# Revit family: VIESSMANN - Vitocell 100-L (CVL.CVLA)
name_source: partatom
category: Wyposażenie mechaniczne
revit_build: Autodesk Revit 2017 (Build: 20160720_1515(x64)
units: mm (PartAtom-declared; Revit-internal decimal feet)

## family parameters
Numer OmniClass = 23.65.35.11.11
Oparty na płaszczyźnie roboczej = Nie
Punkt obliczania pomieszczeń = Nie
Tnij formami wycięć po wczytaniu = Tak
Typ części = Normalny
Tytuł OmniClass = Storage Water Heaters
Współdzielony = Nie
Wymiar okrągłego złącza = Użyj średnicy
Zawsze pionowo = Tak

## types (5) — shared parameters
Autor = https://www.archispace.pl
Ciepła woda użytkowa = 2"
Cyrkulacja = 1 1/4"
Klasa efektywności energetycznej = B
Numer identyfikacyjny produktu = 0256/08-13
Opis = Podgrzewacz pojemnościowy
Opis indeksowy = 0256/08-13
Producent = Viessmann Sp.z.o.o.
URL = https://www.viessmann-projektant.pl
Viessmann Kolor 1 = Viessmann Kolor 1
Viessmann Kolor 2 = Viessmann Kolor 2
Viessmann Kolor 3 = Viessmann Kolor 3
Wlot ciepłej wody użytkowej od strony wymiennika ciepła = 2"
Zimna woda użytkowa = 2"

## per-type parameters (varying)
- Zbiornik CVL 2000L: Ilość ciepła dyżurnego=4.55 kWh/24h; Masa całkowita=444.00 kg; Masa podgrzewacza=483.00 kg; Model=Podgrzewacz pojemnościowy Viessmann Vitocell 100-L CVL 2000L / Hot water storage tank Viessmann Vitocell 100-L CVL 2000L; Odpowietrzanie=1"; Podział=1310 mm  [stored 4.2979 ft]; Pojemność podgrzewacza=2000.0 L; Spust boczny=1 1/2"; Spust dolny=1"; Szerokośc z izolacją cieplną=1477 mm  [stored 4.8458 ft]; Szerokość - bez izolacji cieplnej=1346 mm  [stored 4.41601 ft]; Szerokość - z izolacją cieplną=1477 mm  [stored 4.8458 ft]; Wymiar przechylenia - bez izolacji cieplnej=2390 mm; Wysokośc przyłącza grzałki=564 mm; Wysokość - bez izolacji cieplnej=2392 mm; Wysokość - z izolacją cieplną=2479 mm; Wysokość króćca cwu=1970 mm; Wysokość króćca cwu/wc=1790 mm  [stored 5.8727 ft]; Wysokość króćca cyrkulacji=1603 mm  [stored 5.25919 ft]; Wysokość króćca spustu=124 mm  [stored 0.406824 ft]; Wysokość króćca zimnej wody użytkowej=511 mm; Wysokość z izolacją cieplną=2479 mm; Średnica - bez izolacji cieplnej=1100 mm; Średnica - z izolacją cieplną=1310 mm  [stored 4.2979 ft]; Średnica z izolacją cieplną=1310 mm  [stored 4.2979 ft]
- Zbiornik CVL 500L: Ilość ciepła dyżurnego=1.95 kWh/24h; Masa całkowita=136.00 kg; Masa podgrzewacza=156.00 kg; Model=Podgrzewacz pojemnościowy Viessmann Vitocell 100-L CVL 500L / Hot water storage tank Viessmann Vitocell 100-L CVL 500L; Odpowietrzanie=0"; Podział=859 mm  [stored 2.81824 ft]; Pojemność podgrzewacza=500.0 L; Spust boczny=1 1/4"; Spust dolny=0"; Szerokośc z izolacją cieplną=923 mm  [stored 3.02822 ft]; Szerokość - bez izolacji cieplnej=837 mm  [stored 2.74606 ft]; Szerokość - z izolacją cieplną=923 mm  [stored 3.02822 ft]; Wymiar przechylenia - bez izolacji cieplnej=1860 mm  [stored 6.10236 ft]; Wysokośc przyłącza grzałki=422 mm  [stored 1.38451 ft]; Wysokość - bez izolacji cieplnej=1844 mm  [stored 6.04987 ft]; Wysokość - z izolacją cieplną=1948 mm; Wysokość króćca cwu=1784 mm  [stored 5.85302 ft]; Wysokość króćca cwu/wc=1469 mm  [stored 4.81955 ft]; Wysokość króćca cyrkulacji=1230 mm  [stored 4.03543 ft]; Wysokość króćca spustu=107 mm  [stored 0.35105 ft]; Wysokość króćca zimnej wody użytkowej=384 mm  [stored 1.25984 ft]; Wysokość z izolacją cieplną=1948 mm; Średnica - bez izolacji cieplnej=650 mm  [stored 2.13255 ft]; Średnica - z izolacją cieplną=859 mm  [stored 2.81824 ft]; Średnica z izolacją cieplną=859 mm  [stored 2.81824 ft]
- Zbiornik CVLA 950L: Ilość ciepła dyżurnego=2.48 kWh/24h; Masa całkowita=284.00 kg; Masa podgrzewacza=314.00 kg; Model=Podgrzewacz pojemnościowy Viessmann Vitocell 100-L CVLA 950L / Hot water storage tank Viessmann Vitocell 100-L CVLA 950L; Odpowietrzanie=0"; Podział=1062 mm  [stored 3.48425 ft]; Pojemność podgrzewacza=950.0 L; Spust boczny=1 1/4"; Spust dolny=0"; Szerokośc z izolacją cieplną=1110 mm  [stored 3.64173 ft]; Szerokość - bez izolacji cieplnej=1005 mm  [stored 3.29724 ft]; Szerokość - z izolacją cieplną=1110 mm  [stored 3.64173 ft]; Wymiar przechylenia - bez izolacji cieplnej=2286 mm; Wysokośc przyłącza grzałki=506 mm  [stored 1.6601 ft]; Wysokość - bez izolacji cieplnej=2103 mm; Wysokość - z izolacją cieplną=2197 mm; Wysokość króćca cwu=1752 mm  [stored 5.74803 ft]; Wysokość króćca cwu/wc=1550 mm  [stored 5.0853 ft]; Wysokość króćca cyrkulacji=1285 mm  [stored 4.21588 ft]; Wysokość króćca spustu=79 mm; Wysokość króćca zimnej wody użytkowej=379 mm  [stored 1.24344 ft]; Wysokość z izolacją cieplną=1897 mm; Średnica - bez izolacji cieplnej=790 mm  [stored 2.59186 ft]; Średnica - z izolacją cieplną=1062 mm  [stored 3.48425 ft]; Średnica z izolacją cieplną=1062 mm  [stored 3.48425 ft]
- Zbiornik CVLA 750L: Ilość ciepła dyżurnego=2.28 kWh/24h; Masa całkowita=235.00 kg; Masa podgrzewacza=260.00 kg; Model=Podgrzewacz pojemnościowy Viessmann Vitocell 100-L CVLA 750L / Hot water storage tank Viessmann Vitocell 100-L CVLA 750L; Odpowietrzanie=0"; Podział=1062 mm  [stored 3.48425 ft]; Pojemność podgrzewacza=750.0 L; Spust boczny=1 1/4"; Spust dolny=0"; Szerokośc z izolacją cieplną=1110 mm  [stored 3.64173 ft]; Szerokość - bez izolacji cieplnej=1005 mm  [stored 3.29724 ft]; Szerokość - z izolacją cieplną=1110 mm  [stored 3.64173 ft]; Wymiar przechylenia - bez izolacji cieplnej=1980 mm; Wysokośc przyłącza grzałki=514 mm  [stored 1.68635 ft]; Wysokość - bez izolacji cieplnej=1797 mm  [stored 5.89567 ft]; Wysokość - z izolacją cieplną=1897 mm; Wysokość króćca cwu=1785 mm  [stored 5.8563 ft]; Wysokość króćca cwu/wc=1447 mm  [stored 4.74738 ft]; Wysokość króćca cyrkulacji=1049 mm  [stored 3.4416 ft]; Wysokość króćca spustu=79 mm; Wysokość króćca zimnej wody użytkowej=338 mm  [stored 1.10892 ft]; Wysokość z izolacją cieplną=1897 mm; Średnica - bez izolacji cieplnej=790 mm  [stored 2.59186 ft]; Średnica - z izolacją cieplną=1062 mm  [stored 3.48425 ft]; Średnica z izolacją cieplną=1062 mm  [stored 3.48425 ft]
- Zbiornik CVL 1500L: Ilość ciepła dyżurnego=3.50 kWh/24h; Masa całkowita=372.00 kg; Masa podgrzewacza=406.00 kg; Model=Podgrzewacz pojemnościowy Viessmann Vitocell 100-L CVL 1500L / Hot water storage tank Viessmann Vitocell 100-L CVL 1500L; Odpowietrzanie=1"; Podział=1310 mm  [stored 4.2979 ft]; Pojemność podgrzewacza=1500.0 L; Spust boczny=1 1/2"; Spust dolny=1"; Szerokośc z izolacją cieplną=1477 mm  [stored 4.8458 ft]; Szerokość - bez izolacji cieplnej=1346 mm  [stored 4.41601 ft]; Szerokość - z izolacją cieplną=1477 mm  [stored 4.8458 ft]; Wymiar przechylenia - bez izolacji cieplnej=1955 mm; Wysokośc przyłącza grzałki=564 mm; Wysokość - bez izolacji cieplnej=1951 mm; Wysokość - z izolacją cieplną=2051 mm; Wysokość króćca cwu=1529 mm  [stored 5.0164 ft]; Wysokość króćca cwu/wc=1347 mm  [stored 4.41929 ft]; Wysokość króćca cyrkulacji=1210 mm  [stored 3.96982 ft]; Wysokość króćca spustu=124 mm  [stored 0.406824 ft]; Wysokość króćca zimnej wody użytkowej=511 mm; Wysokość z izolacją cieplną=2051 mm; Średnica - bez izolacji cieplnej=1100 mm; Średnica - z izolacją cieplną=1310 mm  [stored 4.2979 ft]; Średnica z izolacją cieplną=1310 mm  [stored 4.2979 ft]

note: [stored X ft] marks values corroborated as IEEE doubles in the binary element streams (Revit-internal decimal feet)
